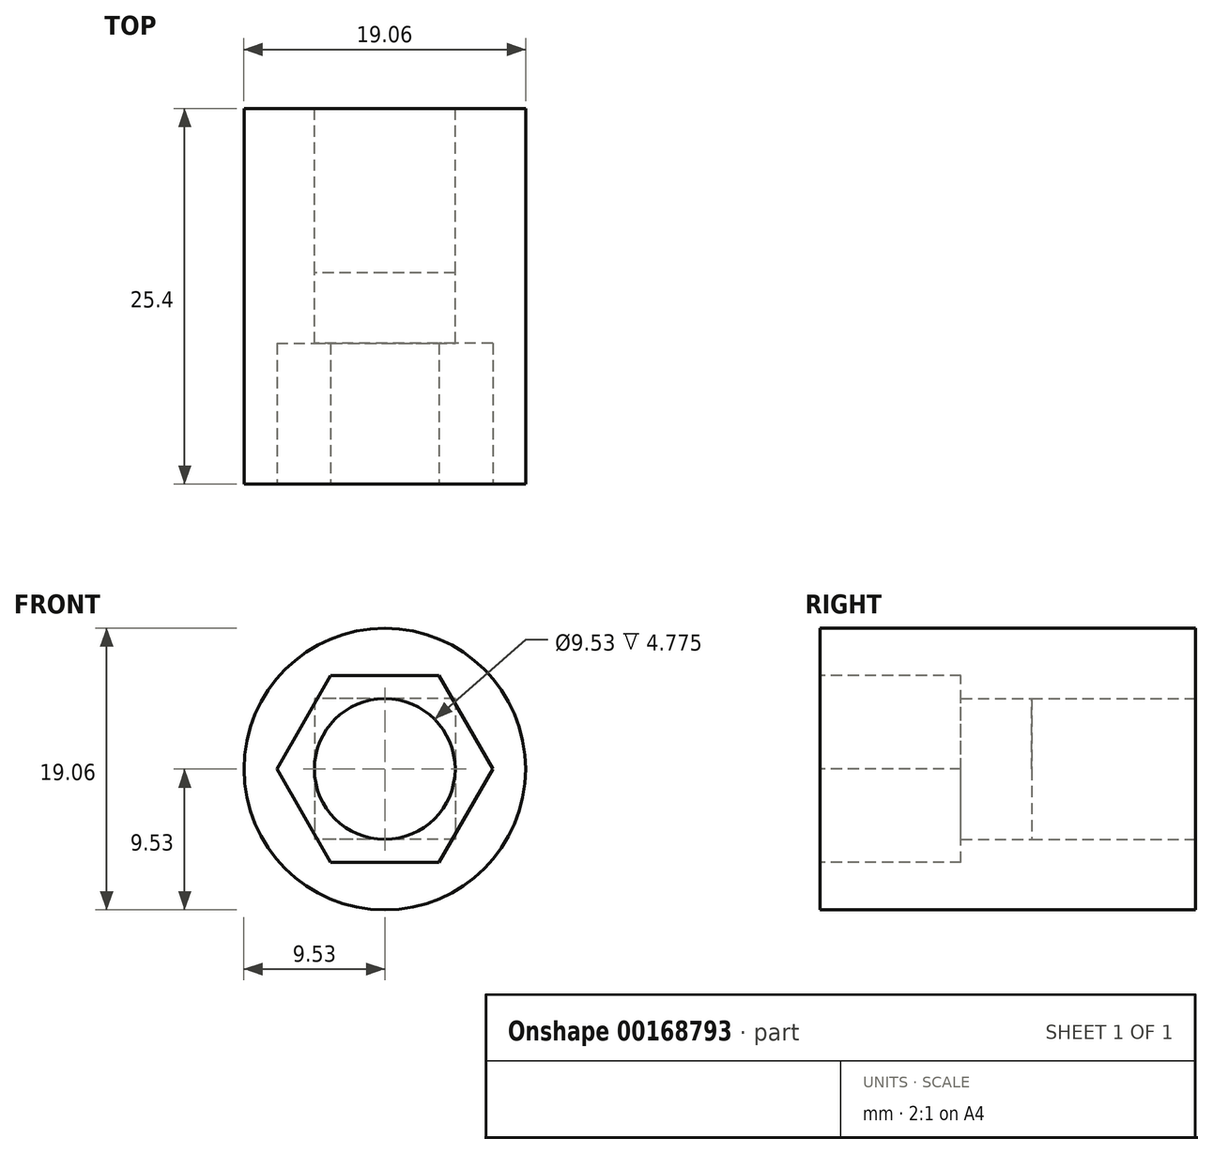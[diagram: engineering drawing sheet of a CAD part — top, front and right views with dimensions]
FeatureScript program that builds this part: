
annotation { "Feature Type Name" : "Feature", "Feature Type Description" : "" }
export const myFeature = defineFeature(function(context is Context, id is Id, definition is map)
    precondition{}
    {
        {
            var Q0;
            Q0=qCreatedBy(makeId("Front.planeOp"),FACE);
            var sketch = newSketch(context, id + "F0", { "sketchPlane" : qUnion([Q0])});
            skCircle(sketch, "E0", {"center": v(0, 0) * mm, "radius": 9.53 * mm});
            skSolve(sketch);
        }
        {
            var Q0;
            Q0 = qSketchRegion(id + "F0", true);
            var Q1;
            Q1=makeQuery(id+"F0.imprint","IMPRINT",FACE,{"disambiguationData":[TD([[makeQuery(id+"F0.imprint","IMPRINT",EDGE,{"derivedFrom":sQuery(id+"F0.wireOp",EDGE,"E0")}),1.0]])]});
            extrude(context, id + "F1", {"entities" : qUnion([Q0, Q1]), "depth" : 25.4 * mm});
        }
        {
            var Q0;
            Q0=qCreatedBy(makeId("Front.planeOp"),FACE);
            var sketch = newSketch(context, id + "F2", { "sketchPlane" : qUnion([Q0])});
            skLineSegment(sketch, "E1.bottom", {"start": v(4.76, 4.76) * mm, "end": v(-4.76, 4.76) * mm});
            skLineSegment(sketch, "E1.top", {"start": v(4.76, -4.76) * mm, "end": v(-4.76, -4.76) * mm});
            skLineSegment(sketch, "E1.left", {"start": v(4.76, 4.76) * mm, "end": v(4.76, -4.76) * mm});
            skLineSegment(sketch, "E1.right", {"start": v(-4.76, 4.76) * mm, "end": v(-4.76, -4.76) * mm});
            skPoint(sketch, "E1.middle", {"position": v(0, 0) * mm});
            skSolve(sketch);
        }
        {
            var Q0;
            Q0=qCreatedBy(makeId("Front.planeOp"),FACE);
            var sketch = newSketch(context, id + "F3", { "sketchPlane" : qUnion([Q0])});
            skCircle(sketch, "E2", {"center": v(0, 0) * mm, "radius": 4.76 * mm});
            skSolve(sketch);
        }
        {
            var Q0;
            Q0 = qSketchRegion(id + "F3", true);
            var Q1;
            Q1=sQuery(id+"F3.wireOp",EDGE,"E2");
            extrude(context, id + "F4", {"entities" : qUnion([Q0]), "operationType" : NewBodyOperationType.REMOVE, "surfaceEntities" : qUnion([Q1]), "endBound" : BoundingType.THROUGH_ALL, "depth" : 25.4 * mm});
        }
        {
            var Q0;
            Q0 = qSketchRegion(id + "F2", true);
            extrude(context, id + "F5", {"entities" : qUnion([Q0]), "operationType" : NewBodyOperationType.REMOVE, "depth" : 11.1 * mm});
        }
        {
            var Q0;
            Q0=makeQuery(id+"F1.opExtrude","CAP_FACE",FACE,{"disambiguationData":[OSD([sQuery(id+"F0.wireOp",EDGE,"E0")])],"isStart":false});
            var sketch = newSketch(context, id + "F6", { "sketchPlane" : qUnion([Q0])});
            skCircle(sketch, "E3.cCircle", {"center": v(0, 0) * mm, "radius": 6.32 * mm, "construction": true});
            skLineSegment(sketch, "E3.0", {"start": v(-3.65, 6.32) * mm, "end": v(3.65, 6.32) * mm});
            skLineSegment(sketch, "E3.1", {"start": v(3.65, 6.32) * mm, "end": v(7.3, 0) * mm});
            skLineSegment(sketch, "E3.2", {"start": v(7.3, 0) * mm, "end": v(3.65, -6.32) * mm});
            skLineSegment(sketch, "E3.3", {"start": v(3.65, -6.32) * mm, "end": v(-3.65, -6.32) * mm});
            skLineSegment(sketch, "E3.4", {"start": v(-3.65, -6.32) * mm, "end": v(-7.3, 0) * mm});
            skLineSegment(sketch, "E3.5", {"start": v(-7.3, 0) * mm, "end": v(-3.65, 6.32) * mm});
            skPoint(sketch, "E3.0.midPoint", {"position": v(0, 6.32) * mm});
            skSolve(sketch);
        }
        {
            var Q0;
            Q0 = qSketchRegion(id + "F6", true);
            extrude(context, id + "F7", {"entities" : qUnion([Q0]), "operationType" : NewBodyOperationType.REMOVE, "oppositeDirection" : true, "depth" : 9.52 * mm});
        }
    });
